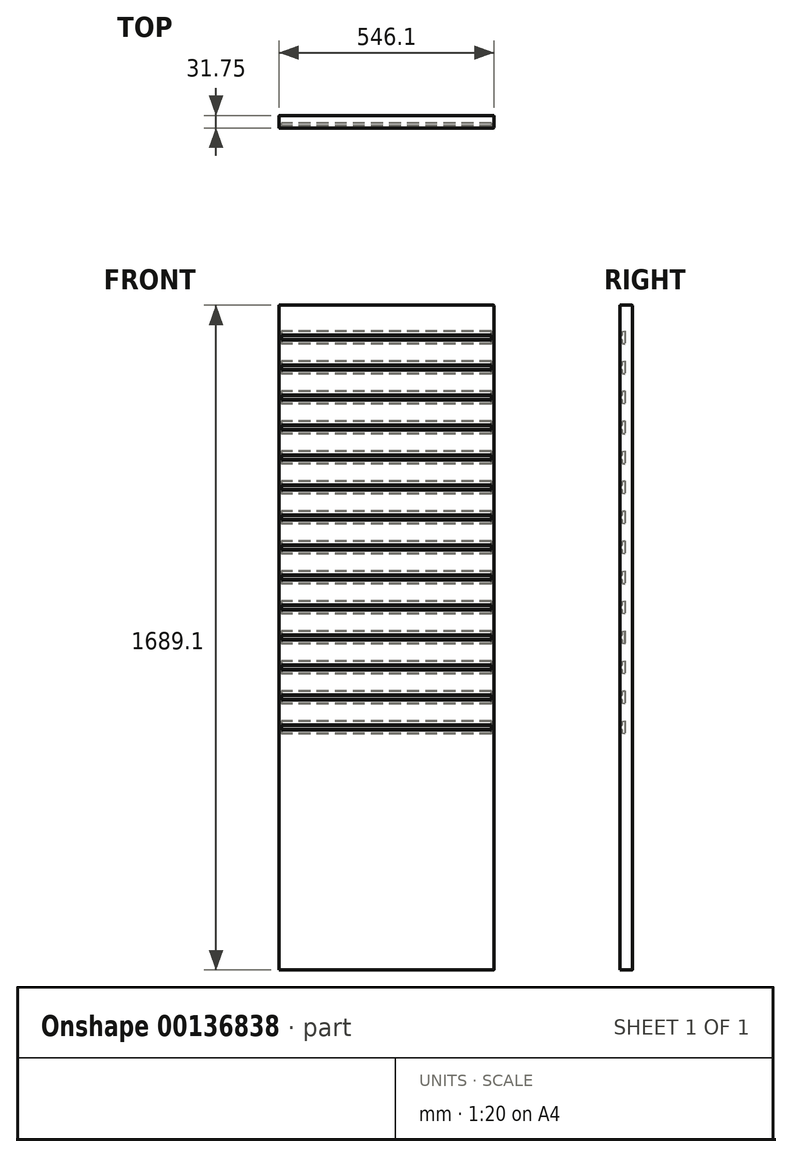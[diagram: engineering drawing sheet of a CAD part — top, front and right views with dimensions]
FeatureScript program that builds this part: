
annotation { "Feature Type Name" : "Feature", "Feature Type Description" : "" }
export const myFeature = defineFeature(function(context is Context, id is Id, definition is map)
    precondition{}
    {
        {
            var Q0;
            Q0=qCreatedBy(makeId("Front.planeOp"),FACE);
            var sketch = newSketch(context, id + "F0", { "sketchPlane" : qUnion([Q0])});
            skLineSegment(sketch, "E0.bottom", {"start": v(266.7, -841.38) * mm, "end": v(-266.7, -841.38) * mm});
            skLineSegment(sketch, "E0.top", {"start": v(266.7, 841.37) * mm, "end": v(-266.7, 841.37) * mm});
            skLineSegment(sketch, "E0.left", {"start": v(266.7, -841.38) * mm, "end": v(266.7, 841.37) * mm});
            skLineSegment(sketch, "E0.right", {"start": v(-266.7, -841.38) * mm, "end": v(-266.7, 841.37) * mm});
            skPoint(sketch, "E0.middle", {"position": v(0, 0) * mm});
            skSolve(sketch);
        }
        {
            var Q0;
            Q0=makeQuery(id+"F0.imprint","IMPRINT",FACE,{"disambiguationData":[TD([[makeQuery(id+"F0.imprint","IMPRINT",EDGE,{"derivedFrom":sQuery(id+"F0.wireOp",EDGE,"E0.bottom")}),-1.0]])]});
            extrude(context, id + "F1", {"entities" : qUnion([Q0]), "oppositeDirection" : true, "depth" : 31.75 * mm});
        }
        {
            var Q0;
            Q0=makeQuery(id+"F1.opExtrude","SWEPT_FACE",FACE,{"disambiguationData":[OSD([sQuery(id+"F0.wireOp",EDGE,"E0.left")])]});
            var sketch = newSketch(context, id + "F2", { "sketchPlane" : qUnion([Q0])});
            skLineSegment(sketch, "E1", {"start": v(-4.76, -4.76) * mm, "end": v(-3.18, -4.76) * mm});
            skLineSegment(sketch, "E2", {"start": v(-6.35, -6.35) * mm, "end": v(-4.76, -4.76) * mm});
            skLineSegment(sketch, "E3", {"start": v(-3.18, -4.76) * mm, "end": v(0, -6.6) * mm});
            skLineSegment(sketch, "E4", {"start": v(-3.18, 4.76) * mm, "end": v(0, 6.6) * mm});
            skLineSegment(sketch, "E5", {"start": v(-4.76, 4.76) * mm, "end": v(-3.18, 4.76) * mm});
            skLineSegment(sketch, "E6", {"start": v(-6.35, 6.35) * mm, "end": v(-4.76, 4.76) * mm});
            skLineSegment(sketch, "E7", {"start": v(0, 14.97) * mm, "end": v(0, 6.6) * mm});
            skLineSegment(sketch, "E8", {"start": v(6.35, 16.67) * mm, "end": v(6.35, -16.67) * mm});
            skLineSegment(sketch, "E9", {"start": v(6.35, -16.67) * mm, "end": v(0, -14.97) * mm});
            skLineSegment(sketch, "E10", {"start": v(0, -6.6) * mm, "end": v(0, -14.97) * mm});
            skLineSegment(sketch, "E11", {"start": v(6.35, 16.67) * mm, "end": v(0, 14.97) * mm});
            skLineSegment(sketch, "E12", {"start": v(-6.35, 6.35) * mm, "end": v(-6.35, -6.35) * mm});
            skSolve(sketch);
        }
        {
            var Q0;
            Q0 = qSketchRegion(id + "F2", true);
            extrude(context, id + "F3", {"entities" : qUnion([Q0]), "depth" : 635 * mm});
        }
        {
            var Q0;
            Q0=makeQuery(id+"F3.opExtrude","CAP_FACE",FACE,{"disambiguationData":[OSD([sQuery(id+"F2.wireOp",EDGE,"E1"),sQuery(id+"F2.wireOp",EDGE,"E2"),sQuery(id+"F2.wireOp",EDGE,"E3"),sQuery(id+"F2.wireOp",EDGE,"E4"),sQuery(id+"F2.wireOp",EDGE,"E5"),sQuery(id+"F2.wireOp",EDGE,"E6"),sQuery(id+"F2.wireOp",EDGE,"E7"),sQuery(id+"F2.wireOp",EDGE,"E9"),sQuery(id+"F2.wireOp",EDGE,"E10"),sQuery(id+"F2.wireOp",EDGE,"E11"),sQuery(id+"F2.wireOp",EDGE,"E8"),sQuery(id+"F2.wireOp",EDGE,"E12")])],"isStart":false});
            var sketch = newSketch(context, id + "F4", { "sketchPlane" : qUnion([Q0])});
            skPoint(sketch, "E13", {"position": v(-6.35, 0) * mm});
            skSolve(sketch);
        }
        {
            var Q0;
            Q0=makeQuery(id+"F1.opExtrude","SWEPT_FACE",FACE,{"disambiguationData":[OSD([sQuery(id+"F0.wireOp",EDGE,"E0.left")])]});
            var sketch = newSketch(context, id + "F5", { "sketchPlane" : qUnion([Q0])});
            skPoint(sketch, "E14", {"position": v(0, 765.17) * mm});
            skPoint(sketch, "E15.0.1.0", {"position": v(0, 688.97) * mm});
            skPoint(sketch, "E15.0.2.0", {"position": v(0, 612.77) * mm});
            skPoint(sketch, "E15.0.3.0", {"position": v(0, 536.57) * mm});
            skPoint(sketch, "E15.0.4.0", {"position": v(0, 460.37) * mm});
            skPoint(sketch, "E15.0.5.0", {"position": v(0, 384.17) * mm});
            skPoint(sketch, "E15.0.6.0", {"position": v(0, 307.97) * mm});
            skPoint(sketch, "E15.0.7.0", {"position": v(0, 231.77) * mm});
            skPoint(sketch, "E15.0.8.0", {"position": v(0, 155.57) * mm});
            skPoint(sketch, "E15.0.9.0", {"position": v(0, 79.37) * mm});
            skLineSegment(sketch, "E15.direction1", {"start": v(0, 765.17) * mm, "end": v(25.4, 765.17) * mm, "construction": true});
            skLineSegment(sketch, "E15.direction2", {"start": v(0, 765.17) * mm, "end": v(0, 688.97) * mm, "construction": true});
            skPoint(sketch, "E16.0.0.10", {"position": v(0, 3.17) * mm});
            skPoint(sketch, "E16.0.0.11", {"position": v(0, -73.03) * mm});
            skPoint(sketch, "E16.0.0.12", {"position": v(0, -149.23) * mm});
            skPoint(sketch, "E16.0.0.13", {"position": v(0, -225.43) * mm});
            skSolve(sketch);
        }
        {
            var Q0;
            Q0=makeQuery(id+"F3.opExtrude","SWEPT_BODY",BODY,{"disambiguationData":[OSD([sQuery(id+"F2.wireOp",EDGE,"E1"),sQuery(id+"F2.wireOp",EDGE,"E2"),sQuery(id+"F2.wireOp",EDGE,"E3"),sQuery(id+"F2.wireOp",EDGE,"E4"),sQuery(id+"F2.wireOp",EDGE,"E5"),sQuery(id+"F2.wireOp",EDGE,"E6"),sQuery(id+"F2.wireOp",EDGE,"E7"),sQuery(id+"F2.wireOp",EDGE,"E9"),sQuery(id+"F2.wireOp",EDGE,"E10"),sQuery(id+"F2.wireOp",EDGE,"E11"),sQuery(id+"F2.wireOp",EDGE,"E8"),sQuery(id+"F2.wireOp",EDGE,"E12")])]});
            var Q1;
            Q1=sQuery(id+"F4.wireOp",VERTEX,"E13");
            var Q2;
            Q2=sQuery(id+"F5.wireOp",VERTEX,"E16.0.0.13");
            transform(context, id + "F6", {"entities" : qUnion([Q0]), "transformType" : TransformType.TRANSLATION_ENTITY, "oppositeDirectionEntity" : false, "transformLine" : qUnion([Q1, Q2]), "makeCopy" : true});
        }
        {
            var Q0;
            Q0=makeQuery(id+"F3.opExtrude","SWEPT_BODY",BODY,{"disambiguationData":[OSD([sQuery(id+"F2.wireOp",EDGE,"E1"),sQuery(id+"F2.wireOp",EDGE,"E2"),sQuery(id+"F2.wireOp",EDGE,"E3"),sQuery(id+"F2.wireOp",EDGE,"E4"),sQuery(id+"F2.wireOp",EDGE,"E5"),sQuery(id+"F2.wireOp",EDGE,"E6"),sQuery(id+"F2.wireOp",EDGE,"E7"),sQuery(id+"F2.wireOp",EDGE,"E9"),sQuery(id+"F2.wireOp",EDGE,"E10"),sQuery(id+"F2.wireOp",EDGE,"E11"),sQuery(id+"F2.wireOp",EDGE,"E8"),sQuery(id+"F2.wireOp",EDGE,"E12")])]});
            var Q1;
            Q1=sQuery(id+"F4.wireOp",VERTEX,"E13");
            var Q2;
            Q2=sQuery(id+"F5.wireOp",VERTEX,"E16.0.0.12");
            transform(context, id + "F7", {"entities" : qUnion([Q0]), "transformType" : TransformType.TRANSLATION_ENTITY, "oppositeDirectionEntity" : false, "transformLine" : qUnion([Q1, Q2]), "makeCopy" : true});
        }
        {
            var Q0;
            Q0=makeQuery(id+"F3.opExtrude","SWEPT_BODY",BODY,{"disambiguationData":[OSD([sQuery(id+"F2.wireOp",EDGE,"E1"),sQuery(id+"F2.wireOp",EDGE,"E2"),sQuery(id+"F2.wireOp",EDGE,"E3"),sQuery(id+"F2.wireOp",EDGE,"E4"),sQuery(id+"F2.wireOp",EDGE,"E5"),sQuery(id+"F2.wireOp",EDGE,"E6"),sQuery(id+"F2.wireOp",EDGE,"E7"),sQuery(id+"F2.wireOp",EDGE,"E9"),sQuery(id+"F2.wireOp",EDGE,"E10"),sQuery(id+"F2.wireOp",EDGE,"E11"),sQuery(id+"F2.wireOp",EDGE,"E8"),sQuery(id+"F2.wireOp",EDGE,"E12")])]});
            var Q1;
            Q1=sQuery(id+"F4.wireOp",VERTEX,"E13");
            var Q2;
            Q2=sQuery(id+"F5.wireOp",VERTEX,"E16.0.0.11");
            transform(context, id + "F8", {"entities" : qUnion([Q0]), "transformType" : TransformType.TRANSLATION_ENTITY, "oppositeDirectionEntity" : false, "transformLine" : qUnion([Q1, Q2]), "makeCopy" : true});
        }
        {
            var Q0;
            Q0=makeQuery(id+"F3.opExtrude","SWEPT_BODY",BODY,{"disambiguationData":[OSD([sQuery(id+"F2.wireOp",EDGE,"E1"),sQuery(id+"F2.wireOp",EDGE,"E2"),sQuery(id+"F2.wireOp",EDGE,"E3"),sQuery(id+"F2.wireOp",EDGE,"E4"),sQuery(id+"F2.wireOp",EDGE,"E5"),sQuery(id+"F2.wireOp",EDGE,"E6"),sQuery(id+"F2.wireOp",EDGE,"E7"),sQuery(id+"F2.wireOp",EDGE,"E9"),sQuery(id+"F2.wireOp",EDGE,"E10"),sQuery(id+"F2.wireOp",EDGE,"E11"),sQuery(id+"F2.wireOp",EDGE,"E8"),sQuery(id+"F2.wireOp",EDGE,"E12")])]});
            var Q1;
            Q1=sQuery(id+"F4.wireOp",VERTEX,"E13");
            var Q2;
            Q2=sQuery(id+"F5.wireOp",VERTEX,"E16.0.0.10");
            transform(context, id + "F9", {"entities" : qUnion([Q0]), "transformType" : TransformType.TRANSLATION_ENTITY, "oppositeDirectionEntity" : false, "transformLine" : qUnion([Q1, Q2]), "makeCopy" : true});
        }
        {
            var Q0;
            Q0=makeQuery(id+"F3.opExtrude","SWEPT_BODY",BODY,{"disambiguationData":[OSD([sQuery(id+"F2.wireOp",EDGE,"E1"),sQuery(id+"F2.wireOp",EDGE,"E2"),sQuery(id+"F2.wireOp",EDGE,"E3"),sQuery(id+"F2.wireOp",EDGE,"E4"),sQuery(id+"F2.wireOp",EDGE,"E5"),sQuery(id+"F2.wireOp",EDGE,"E6"),sQuery(id+"F2.wireOp",EDGE,"E7"),sQuery(id+"F2.wireOp",EDGE,"E9"),sQuery(id+"F2.wireOp",EDGE,"E10"),sQuery(id+"F2.wireOp",EDGE,"E11"),sQuery(id+"F2.wireOp",EDGE,"E8"),sQuery(id+"F2.wireOp",EDGE,"E12")])]});
            var Q1;
            Q1=sQuery(id+"F4.wireOp",VERTEX,"E13");
            var Q2;
            Q2=sQuery(id+"F5.wireOp",VERTEX,"E15.0.9.0");
            transform(context, id + "F10", {"entities" : qUnion([Q0]), "transformType" : TransformType.TRANSLATION_ENTITY, "oppositeDirectionEntity" : false, "transformLine" : qUnion([Q1, Q2]), "makeCopy" : true});
        }
        {
            var Q0;
            Q0=makeQuery(id+"F3.opExtrude","SWEPT_BODY",BODY,{"disambiguationData":[OSD([sQuery(id+"F2.wireOp",EDGE,"E1"),sQuery(id+"F2.wireOp",EDGE,"E2"),sQuery(id+"F2.wireOp",EDGE,"E3"),sQuery(id+"F2.wireOp",EDGE,"E4"),sQuery(id+"F2.wireOp",EDGE,"E5"),sQuery(id+"F2.wireOp",EDGE,"E6"),sQuery(id+"F2.wireOp",EDGE,"E7"),sQuery(id+"F2.wireOp",EDGE,"E9"),sQuery(id+"F2.wireOp",EDGE,"E10"),sQuery(id+"F2.wireOp",EDGE,"E11"),sQuery(id+"F2.wireOp",EDGE,"E8"),sQuery(id+"F2.wireOp",EDGE,"E12")])]});
            var Q1;
            Q1=sQuery(id+"F4.wireOp",VERTEX,"E13");
            var Q2;
            Q2=sQuery(id+"F5.wireOp",VERTEX,"E15.0.8.0");
            transform(context, id + "F11", {"entities" : qUnion([Q0]), "transformType" : TransformType.TRANSLATION_ENTITY, "oppositeDirectionEntity" : false, "transformLine" : qUnion([Q1, Q2]), "makeCopy" : true});
        }
        {
            var Q0;
            Q0=makeQuery(id+"F3.opExtrude","SWEPT_BODY",BODY,{"disambiguationData":[OSD([sQuery(id+"F2.wireOp",EDGE,"E1"),sQuery(id+"F2.wireOp",EDGE,"E2"),sQuery(id+"F2.wireOp",EDGE,"E3"),sQuery(id+"F2.wireOp",EDGE,"E4"),sQuery(id+"F2.wireOp",EDGE,"E5"),sQuery(id+"F2.wireOp",EDGE,"E6"),sQuery(id+"F2.wireOp",EDGE,"E7"),sQuery(id+"F2.wireOp",EDGE,"E9"),sQuery(id+"F2.wireOp",EDGE,"E10"),sQuery(id+"F2.wireOp",EDGE,"E11"),sQuery(id+"F2.wireOp",EDGE,"E8"),sQuery(id+"F2.wireOp",EDGE,"E12")])]});
            var Q1;
            Q1=sQuery(id+"F4.wireOp",VERTEX,"E13");
            var Q2;
            Q2=sQuery(id+"F5.wireOp",VERTEX,"E15.0.7.0");
            transform(context, id + "F12", {"entities" : qUnion([Q0]), "transformType" : TransformType.TRANSLATION_ENTITY, "oppositeDirectionEntity" : false, "transformLine" : qUnion([Q1, Q2]), "makeCopy" : true});
        }
        {
            var Q0;
            Q0=makeQuery(id+"F3.opExtrude","SWEPT_BODY",BODY,{"disambiguationData":[OSD([sQuery(id+"F2.wireOp",EDGE,"E1"),sQuery(id+"F2.wireOp",EDGE,"E2"),sQuery(id+"F2.wireOp",EDGE,"E3"),sQuery(id+"F2.wireOp",EDGE,"E4"),sQuery(id+"F2.wireOp",EDGE,"E5"),sQuery(id+"F2.wireOp",EDGE,"E6"),sQuery(id+"F2.wireOp",EDGE,"E7"),sQuery(id+"F2.wireOp",EDGE,"E9"),sQuery(id+"F2.wireOp",EDGE,"E10"),sQuery(id+"F2.wireOp",EDGE,"E11"),sQuery(id+"F2.wireOp",EDGE,"E8"),sQuery(id+"F2.wireOp",EDGE,"E12")])]});
            var Q1;
            Q1=sQuery(id+"F4.wireOp",VERTEX,"E13");
            var Q2;
            Q2=sQuery(id+"F5.wireOp",VERTEX,"E15.0.6.0");
            transform(context, id + "F13", {"entities" : qUnion([Q0]), "transformType" : TransformType.TRANSLATION_ENTITY, "oppositeDirectionEntity" : false, "transformLine" : qUnion([Q1, Q2]), "makeCopy" : true});
        }
        {
            var Q0;
            Q0=makeQuery(id+"F3.opExtrude","SWEPT_BODY",BODY,{"disambiguationData":[OSD([sQuery(id+"F2.wireOp",EDGE,"E1"),sQuery(id+"F2.wireOp",EDGE,"E2"),sQuery(id+"F2.wireOp",EDGE,"E3"),sQuery(id+"F2.wireOp",EDGE,"E4"),sQuery(id+"F2.wireOp",EDGE,"E5"),sQuery(id+"F2.wireOp",EDGE,"E6"),sQuery(id+"F2.wireOp",EDGE,"E7"),sQuery(id+"F2.wireOp",EDGE,"E9"),sQuery(id+"F2.wireOp",EDGE,"E10"),sQuery(id+"F2.wireOp",EDGE,"E11"),sQuery(id+"F2.wireOp",EDGE,"E8"),sQuery(id+"F2.wireOp",EDGE,"E12")])]});
            var Q1;
            Q1=sQuery(id+"F4.wireOp",VERTEX,"E13");
            var Q2;
            Q2=sQuery(id+"F5.wireOp",VERTEX,"E15.0.5.0");
            transform(context, id + "F14", {"entities" : qUnion([Q0]), "transformType" : TransformType.TRANSLATION_ENTITY, "oppositeDirectionEntity" : false, "transformLine" : qUnion([Q1, Q2]), "makeCopy" : true});
        }
        {
            var Q0;
            Q0=makeQuery(id+"F3.opExtrude","SWEPT_BODY",BODY,{"disambiguationData":[OSD([sQuery(id+"F2.wireOp",EDGE,"E1"),sQuery(id+"F2.wireOp",EDGE,"E2"),sQuery(id+"F2.wireOp",EDGE,"E3"),sQuery(id+"F2.wireOp",EDGE,"E4"),sQuery(id+"F2.wireOp",EDGE,"E5"),sQuery(id+"F2.wireOp",EDGE,"E6"),sQuery(id+"F2.wireOp",EDGE,"E7"),sQuery(id+"F2.wireOp",EDGE,"E9"),sQuery(id+"F2.wireOp",EDGE,"E10"),sQuery(id+"F2.wireOp",EDGE,"E11"),sQuery(id+"F2.wireOp",EDGE,"E8"),sQuery(id+"F2.wireOp",EDGE,"E12")])]});
            var Q1;
            Q1=sQuery(id+"F4.wireOp",VERTEX,"E13");
            var Q2;
            Q2=sQuery(id+"F5.wireOp",VERTEX,"E15.0.4.0");
            transform(context, id + "F15", {"entities" : qUnion([Q0]), "transformType" : TransformType.TRANSLATION_ENTITY, "oppositeDirectionEntity" : false, "transformLine" : qUnion([Q1, Q2]), "makeCopy" : true});
        }
        {
            var Q0;
            Q0=makeQuery(id+"F3.opExtrude","SWEPT_BODY",BODY,{"disambiguationData":[OSD([sQuery(id+"F2.wireOp",EDGE,"E1"),sQuery(id+"F2.wireOp",EDGE,"E2"),sQuery(id+"F2.wireOp",EDGE,"E3"),sQuery(id+"F2.wireOp",EDGE,"E4"),sQuery(id+"F2.wireOp",EDGE,"E5"),sQuery(id+"F2.wireOp",EDGE,"E6"),sQuery(id+"F2.wireOp",EDGE,"E7"),sQuery(id+"F2.wireOp",EDGE,"E9"),sQuery(id+"F2.wireOp",EDGE,"E10"),sQuery(id+"F2.wireOp",EDGE,"E11"),sQuery(id+"F2.wireOp",EDGE,"E8"),sQuery(id+"F2.wireOp",EDGE,"E12")])]});
            var Q1;
            Q1=sQuery(id+"F4.wireOp",VERTEX,"E13");
            var Q2;
            Q2=sQuery(id+"F5.wireOp",VERTEX,"E15.0.3.0");
            transform(context, id + "F16", {"entities" : qUnion([Q0]), "transformType" : TransformType.TRANSLATION_ENTITY, "oppositeDirectionEntity" : false, "transformLine" : qUnion([Q1, Q2]), "makeCopy" : true});
        }
        {
            var Q0;
            Q0=makeQuery(id+"F3.opExtrude","SWEPT_BODY",BODY,{"disambiguationData":[OSD([sQuery(id+"F2.wireOp",EDGE,"E1"),sQuery(id+"F2.wireOp",EDGE,"E2"),sQuery(id+"F2.wireOp",EDGE,"E3"),sQuery(id+"F2.wireOp",EDGE,"E4"),sQuery(id+"F2.wireOp",EDGE,"E5"),sQuery(id+"F2.wireOp",EDGE,"E6"),sQuery(id+"F2.wireOp",EDGE,"E7"),sQuery(id+"F2.wireOp",EDGE,"E9"),sQuery(id+"F2.wireOp",EDGE,"E10"),sQuery(id+"F2.wireOp",EDGE,"E11"),sQuery(id+"F2.wireOp",EDGE,"E8"),sQuery(id+"F2.wireOp",EDGE,"E12")])]});
            var Q1;
            Q1=sQuery(id+"F4.wireOp",VERTEX,"E13");
            var Q2;
            Q2=sQuery(id+"F5.wireOp",VERTEX,"E15.0.2.0");
            transform(context, id + "F17", {"entities" : qUnion([Q0]), "transformType" : TransformType.TRANSLATION_ENTITY, "oppositeDirectionEntity" : false, "transformLine" : qUnion([Q1, Q2]), "makeCopy" : true});
        }
        {
            var Q0;
            Q0=makeQuery(id+"F3.opExtrude","SWEPT_BODY",BODY,{"disambiguationData":[OSD([sQuery(id+"F2.wireOp",EDGE,"E1"),sQuery(id+"F2.wireOp",EDGE,"E2"),sQuery(id+"F2.wireOp",EDGE,"E3"),sQuery(id+"F2.wireOp",EDGE,"E4"),sQuery(id+"F2.wireOp",EDGE,"E5"),sQuery(id+"F2.wireOp",EDGE,"E6"),sQuery(id+"F2.wireOp",EDGE,"E7"),sQuery(id+"F2.wireOp",EDGE,"E9"),sQuery(id+"F2.wireOp",EDGE,"E10"),sQuery(id+"F2.wireOp",EDGE,"E11"),sQuery(id+"F2.wireOp",EDGE,"E8"),sQuery(id+"F2.wireOp",EDGE,"E12")])]});
            var Q1;
            Q1=sQuery(id+"F4.wireOp",VERTEX,"E13");
            var Q2;
            Q2=sQuery(id+"F5.wireOp",VERTEX,"E15.0.1.0");
            transform(context, id + "F18", {"entities" : qUnion([Q0]), "transformType" : TransformType.TRANSLATION_ENTITY, "oppositeDirectionEntity" : false, "transformLine" : qUnion([Q1, Q2]), "makeCopy" : true});
        }
        {
            var Q0;
            Q0=makeQuery(id+"F3.opExtrude","SWEPT_BODY",BODY,{"disambiguationData":[OSD([sQuery(id+"F2.wireOp",EDGE,"E1"),sQuery(id+"F2.wireOp",EDGE,"E2"),sQuery(id+"F2.wireOp",EDGE,"E3"),sQuery(id+"F2.wireOp",EDGE,"E4"),sQuery(id+"F2.wireOp",EDGE,"E5"),sQuery(id+"F2.wireOp",EDGE,"E6"),sQuery(id+"F2.wireOp",EDGE,"E7"),sQuery(id+"F2.wireOp",EDGE,"E9"),sQuery(id+"F2.wireOp",EDGE,"E10"),sQuery(id+"F2.wireOp",EDGE,"E11"),sQuery(id+"F2.wireOp",EDGE,"E8"),sQuery(id+"F2.wireOp",EDGE,"E12")])]});
            var Q1;
            Q1=sQuery(id+"F4.wireOp",VERTEX,"E13");
            var Q2;
            Q2=sQuery(id+"F5.wireOp",VERTEX,"E14");
            transform(context, id + "F19", {"entities" : qUnion([Q0]), "transformType" : TransformType.TRANSLATION_ENTITY, "oppositeDirectionEntity" : false, "transformLine" : qUnion([Q1, Q2]), "makeCopy" : false});
        }
        {
            var Q0;
            Q0=makeQuery(id+"F3.opExtrude","SWEPT_BODY",BODY,{"disambiguationData":[OSD([sQuery(id+"F2.wireOp",EDGE,"E1"),sQuery(id+"F2.wireOp",EDGE,"E2"),sQuery(id+"F2.wireOp",EDGE,"E3"),sQuery(id+"F2.wireOp",EDGE,"E4"),sQuery(id+"F2.wireOp",EDGE,"E5"),sQuery(id+"F2.wireOp",EDGE,"E6"),sQuery(id+"F2.wireOp",EDGE,"E7"),sQuery(id+"F2.wireOp",EDGE,"E9"),sQuery(id+"F2.wireOp",EDGE,"E10"),sQuery(id+"F2.wireOp",EDGE,"E11"),sQuery(id+"F2.wireOp",EDGE,"E8"),sQuery(id+"F2.wireOp",EDGE,"E12")])]});
            var Q1;
            Q1=makeQuery(id+"F18.opPattern","COPY",BODY,{"derivedFrom":makeQuery(id+"F3.opExtrude","SWEPT_BODY",BODY,{"disambiguationData":[OSD([sQuery(id+"F2.wireOp",EDGE,"E1"),sQuery(id+"F2.wireOp",EDGE,"E2"),sQuery(id+"F2.wireOp",EDGE,"E3"),sQuery(id+"F2.wireOp",EDGE,"E4"),sQuery(id+"F2.wireOp",EDGE,"E5"),sQuery(id+"F2.wireOp",EDGE,"E6"),sQuery(id+"F2.wireOp",EDGE,"E7"),sQuery(id+"F2.wireOp",EDGE,"E9"),sQuery(id+"F2.wireOp",EDGE,"E10"),sQuery(id+"F2.wireOp",EDGE,"E11"),sQuery(id+"F2.wireOp",EDGE,"E8"),sQuery(id+"F2.wireOp",EDGE,"E12")])]}),"instanceName":"1"});
            var Q2;
            Q2=makeQuery(id+"F17.opPattern","COPY",BODY,{"derivedFrom":makeQuery(id+"F3.opExtrude","SWEPT_BODY",BODY,{"disambiguationData":[OSD([sQuery(id+"F2.wireOp",EDGE,"E1"),sQuery(id+"F2.wireOp",EDGE,"E2"),sQuery(id+"F2.wireOp",EDGE,"E3"),sQuery(id+"F2.wireOp",EDGE,"E4"),sQuery(id+"F2.wireOp",EDGE,"E5"),sQuery(id+"F2.wireOp",EDGE,"E6"),sQuery(id+"F2.wireOp",EDGE,"E7"),sQuery(id+"F2.wireOp",EDGE,"E9"),sQuery(id+"F2.wireOp",EDGE,"E10"),sQuery(id+"F2.wireOp",EDGE,"E11"),sQuery(id+"F2.wireOp",EDGE,"E8"),sQuery(id+"F2.wireOp",EDGE,"E12")])]}),"instanceName":"1"});
            var Q3;
            Q3=makeQuery(id+"F16.opPattern","COPY",BODY,{"derivedFrom":makeQuery(id+"F3.opExtrude","SWEPT_BODY",BODY,{"disambiguationData":[OSD([sQuery(id+"F2.wireOp",EDGE,"E1"),sQuery(id+"F2.wireOp",EDGE,"E2"),sQuery(id+"F2.wireOp",EDGE,"E3"),sQuery(id+"F2.wireOp",EDGE,"E4"),sQuery(id+"F2.wireOp",EDGE,"E5"),sQuery(id+"F2.wireOp",EDGE,"E6"),sQuery(id+"F2.wireOp",EDGE,"E7"),sQuery(id+"F2.wireOp",EDGE,"E9"),sQuery(id+"F2.wireOp",EDGE,"E10"),sQuery(id+"F2.wireOp",EDGE,"E11"),sQuery(id+"F2.wireOp",EDGE,"E8"),sQuery(id+"F2.wireOp",EDGE,"E12")])]}),"instanceName":"1"});
            var Q4;
            Q4=makeQuery(id+"F15.opPattern","COPY",BODY,{"derivedFrom":makeQuery(id+"F3.opExtrude","SWEPT_BODY",BODY,{"disambiguationData":[OSD([sQuery(id+"F2.wireOp",EDGE,"E1"),sQuery(id+"F2.wireOp",EDGE,"E2"),sQuery(id+"F2.wireOp",EDGE,"E3"),sQuery(id+"F2.wireOp",EDGE,"E4"),sQuery(id+"F2.wireOp",EDGE,"E5"),sQuery(id+"F2.wireOp",EDGE,"E6"),sQuery(id+"F2.wireOp",EDGE,"E7"),sQuery(id+"F2.wireOp",EDGE,"E9"),sQuery(id+"F2.wireOp",EDGE,"E10"),sQuery(id+"F2.wireOp",EDGE,"E11"),sQuery(id+"F2.wireOp",EDGE,"E8"),sQuery(id+"F2.wireOp",EDGE,"E12")])]}),"instanceName":"1"});
            var Q5;
            Q5=makeQuery(id+"F14.opPattern","COPY",BODY,{"derivedFrom":makeQuery(id+"F3.opExtrude","SWEPT_BODY",BODY,{"disambiguationData":[OSD([sQuery(id+"F2.wireOp",EDGE,"E1"),sQuery(id+"F2.wireOp",EDGE,"E2"),sQuery(id+"F2.wireOp",EDGE,"E3"),sQuery(id+"F2.wireOp",EDGE,"E4"),sQuery(id+"F2.wireOp",EDGE,"E5"),sQuery(id+"F2.wireOp",EDGE,"E6"),sQuery(id+"F2.wireOp",EDGE,"E7"),sQuery(id+"F2.wireOp",EDGE,"E9"),sQuery(id+"F2.wireOp",EDGE,"E10"),sQuery(id+"F2.wireOp",EDGE,"E11"),sQuery(id+"F2.wireOp",EDGE,"E8"),sQuery(id+"F2.wireOp",EDGE,"E12")])]}),"instanceName":"1"});
            var Q6;
            Q6=makeQuery(id+"F13.opPattern","COPY",BODY,{"derivedFrom":makeQuery(id+"F3.opExtrude","SWEPT_BODY",BODY,{"disambiguationData":[OSD([sQuery(id+"F2.wireOp",EDGE,"E1"),sQuery(id+"F2.wireOp",EDGE,"E2"),sQuery(id+"F2.wireOp",EDGE,"E3"),sQuery(id+"F2.wireOp",EDGE,"E4"),sQuery(id+"F2.wireOp",EDGE,"E5"),sQuery(id+"F2.wireOp",EDGE,"E6"),sQuery(id+"F2.wireOp",EDGE,"E7"),sQuery(id+"F2.wireOp",EDGE,"E9"),sQuery(id+"F2.wireOp",EDGE,"E10"),sQuery(id+"F2.wireOp",EDGE,"E11"),sQuery(id+"F2.wireOp",EDGE,"E8"),sQuery(id+"F2.wireOp",EDGE,"E12")])]}),"instanceName":"1"});
            var Q7;
            Q7=makeQuery(id+"F12.opPattern","COPY",BODY,{"derivedFrom":makeQuery(id+"F3.opExtrude","SWEPT_BODY",BODY,{"disambiguationData":[OSD([sQuery(id+"F2.wireOp",EDGE,"E1"),sQuery(id+"F2.wireOp",EDGE,"E2"),sQuery(id+"F2.wireOp",EDGE,"E3"),sQuery(id+"F2.wireOp",EDGE,"E4"),sQuery(id+"F2.wireOp",EDGE,"E5"),sQuery(id+"F2.wireOp",EDGE,"E6"),sQuery(id+"F2.wireOp",EDGE,"E7"),sQuery(id+"F2.wireOp",EDGE,"E9"),sQuery(id+"F2.wireOp",EDGE,"E10"),sQuery(id+"F2.wireOp",EDGE,"E11"),sQuery(id+"F2.wireOp",EDGE,"E8"),sQuery(id+"F2.wireOp",EDGE,"E12")])]}),"instanceName":"1"});
            var Q8;
            Q8=makeQuery(id+"F11.opPattern","COPY",BODY,{"derivedFrom":makeQuery(id+"F3.opExtrude","SWEPT_BODY",BODY,{"disambiguationData":[OSD([sQuery(id+"F2.wireOp",EDGE,"E1"),sQuery(id+"F2.wireOp",EDGE,"E2"),sQuery(id+"F2.wireOp",EDGE,"E3"),sQuery(id+"F2.wireOp",EDGE,"E4"),sQuery(id+"F2.wireOp",EDGE,"E5"),sQuery(id+"F2.wireOp",EDGE,"E6"),sQuery(id+"F2.wireOp",EDGE,"E7"),sQuery(id+"F2.wireOp",EDGE,"E9"),sQuery(id+"F2.wireOp",EDGE,"E10"),sQuery(id+"F2.wireOp",EDGE,"E11"),sQuery(id+"F2.wireOp",EDGE,"E8"),sQuery(id+"F2.wireOp",EDGE,"E12")])]}),"instanceName":"1"});
            var Q9;
            Q9=makeQuery(id+"F10.opPattern","COPY",BODY,{"derivedFrom":makeQuery(id+"F3.opExtrude","SWEPT_BODY",BODY,{"disambiguationData":[OSD([sQuery(id+"F2.wireOp",EDGE,"E1"),sQuery(id+"F2.wireOp",EDGE,"E2"),sQuery(id+"F2.wireOp",EDGE,"E3"),sQuery(id+"F2.wireOp",EDGE,"E4"),sQuery(id+"F2.wireOp",EDGE,"E5"),sQuery(id+"F2.wireOp",EDGE,"E6"),sQuery(id+"F2.wireOp",EDGE,"E7"),sQuery(id+"F2.wireOp",EDGE,"E9"),sQuery(id+"F2.wireOp",EDGE,"E10"),sQuery(id+"F2.wireOp",EDGE,"E11"),sQuery(id+"F2.wireOp",EDGE,"E8"),sQuery(id+"F2.wireOp",EDGE,"E12")])]}),"instanceName":"1"});
            var Q10;
            Q10=makeQuery(id+"F9.opPattern","COPY",BODY,{"derivedFrom":makeQuery(id+"F3.opExtrude","SWEPT_BODY",BODY,{"disambiguationData":[OSD([sQuery(id+"F2.wireOp",EDGE,"E1"),sQuery(id+"F2.wireOp",EDGE,"E2"),sQuery(id+"F2.wireOp",EDGE,"E3"),sQuery(id+"F2.wireOp",EDGE,"E4"),sQuery(id+"F2.wireOp",EDGE,"E5"),sQuery(id+"F2.wireOp",EDGE,"E6"),sQuery(id+"F2.wireOp",EDGE,"E7"),sQuery(id+"F2.wireOp",EDGE,"E9"),sQuery(id+"F2.wireOp",EDGE,"E10"),sQuery(id+"F2.wireOp",EDGE,"E11"),sQuery(id+"F2.wireOp",EDGE,"E8"),sQuery(id+"F2.wireOp",EDGE,"E12")])]}),"instanceName":"1"});
            var Q11;
            Q11=makeQuery(id+"F8.opPattern","COPY",BODY,{"derivedFrom":makeQuery(id+"F3.opExtrude","SWEPT_BODY",BODY,{"disambiguationData":[OSD([sQuery(id+"F2.wireOp",EDGE,"E1"),sQuery(id+"F2.wireOp",EDGE,"E2"),sQuery(id+"F2.wireOp",EDGE,"E3"),sQuery(id+"F2.wireOp",EDGE,"E4"),sQuery(id+"F2.wireOp",EDGE,"E5"),sQuery(id+"F2.wireOp",EDGE,"E6"),sQuery(id+"F2.wireOp",EDGE,"E7"),sQuery(id+"F2.wireOp",EDGE,"E9"),sQuery(id+"F2.wireOp",EDGE,"E10"),sQuery(id+"F2.wireOp",EDGE,"E11"),sQuery(id+"F2.wireOp",EDGE,"E8"),sQuery(id+"F2.wireOp",EDGE,"E12")])]}),"instanceName":"1"});
            var Q12;
            Q12=makeQuery(id+"F7.opPattern","COPY",BODY,{"derivedFrom":makeQuery(id+"F3.opExtrude","SWEPT_BODY",BODY,{"disambiguationData":[OSD([sQuery(id+"F2.wireOp",EDGE,"E1"),sQuery(id+"F2.wireOp",EDGE,"E2"),sQuery(id+"F2.wireOp",EDGE,"E3"),sQuery(id+"F2.wireOp",EDGE,"E4"),sQuery(id+"F2.wireOp",EDGE,"E5"),sQuery(id+"F2.wireOp",EDGE,"E6"),sQuery(id+"F2.wireOp",EDGE,"E7"),sQuery(id+"F2.wireOp",EDGE,"E9"),sQuery(id+"F2.wireOp",EDGE,"E10"),sQuery(id+"F2.wireOp",EDGE,"E11"),sQuery(id+"F2.wireOp",EDGE,"E8"),sQuery(id+"F2.wireOp",EDGE,"E12")])]}),"instanceName":"1"});
            var Q13;
            Q13=makeQuery(id+"F6.opPattern","COPY",BODY,{"derivedFrom":makeQuery(id+"F3.opExtrude","SWEPT_BODY",BODY,{"disambiguationData":[OSD([sQuery(id+"F2.wireOp",EDGE,"E1"),sQuery(id+"F2.wireOp",EDGE,"E2"),sQuery(id+"F2.wireOp",EDGE,"E3"),sQuery(id+"F2.wireOp",EDGE,"E4"),sQuery(id+"F2.wireOp",EDGE,"E5"),sQuery(id+"F2.wireOp",EDGE,"E6"),sQuery(id+"F2.wireOp",EDGE,"E7"),sQuery(id+"F2.wireOp",EDGE,"E9"),sQuery(id+"F2.wireOp",EDGE,"E10"),sQuery(id+"F2.wireOp",EDGE,"E11"),sQuery(id+"F2.wireOp",EDGE,"E8"),sQuery(id+"F2.wireOp",EDGE,"E12")])]}),"instanceName":"1"});
            var Q14;
            Q14=makeQuery(id+"F1.opExtrude","SWEPT_BODY",BODY,{"disambiguationData":[OSD([sQuery(id+"F0.wireOp",EDGE,"E0.bottom"),sQuery(id+"F0.wireOp",EDGE,"E0.top"),sQuery(id+"F0.wireOp",EDGE,"E0.left"),sQuery(id+"F0.wireOp",EDGE,"E0.right")])]});
            booleanBodies(context, id + "F20", {"operationType" : BooleanOperationType.SUBTRACTION, "tools" : qUnion([Q0, Q1, Q2, Q3, Q4, Q5, Q6, Q7, Q8, Q9, Q10, Q11, Q12, Q13]), "targets" : qUnion([Q14])});
        }
        {
            var Q0;
            Q0=makeQuery(id+"F1.opExtrude","SWEPT_FACE",FACE,{"disambiguationData":[OSD([sQuery(id+"F0.wireOp",EDGE,"E0.left")])]});
            var sketch = newSketch(context, id + "F21", { "sketchPlane" : qUnion([Q0])});
            skLineSegment(sketch, "E17.bottom", {"start": v(31.75, -841.38) * mm, "end": v(0, -841.38) * mm});
            skLineSegment(sketch, "E17.top", {"start": v(31.75, 841.37) * mm, "end": v(0, 841.37) * mm});
            skLineSegment(sketch, "E17.left", {"start": v(31.75, -841.38) * mm, "end": v(31.75, 841.37) * mm});
            skLineSegment(sketch, "E17.right", {"start": v(0, -841.38) * mm, "end": v(0, 841.37) * mm});
            skSolve(sketch);
        }
        {
            var Q0;
            Q0 = qSketchRegion(id + "F21", true);
            extrude(context, id + "F22", {"entities" : qUnion([Q0]), "operationType" : NewBodyOperationType.ADD, "depth" : 6.35 * mm});
        }
        {
            var Q0;
            Q0=makeQuery(id+"F1.opExtrude","SWEPT_FACE",FACE,{"disambiguationData":[OSD([sQuery(id+"F0.wireOp",EDGE,"E0.right")])]});
            var sketch = newSketch(context, id + "F23", { "sketchPlane" : qUnion([Q0])});
            skLineSegment(sketch, "E18.bottom", {"start": v(-31.75, 841.37) * mm, "end": v(0, 841.37) * mm});
            skLineSegment(sketch, "E18.top", {"start": v(-31.75, -841.38) * mm, "end": v(0, -841.38) * mm});
            skLineSegment(sketch, "E18.left", {"start": v(-31.75, 841.37) * mm, "end": v(-31.75, -841.38) * mm});
            skLineSegment(sketch, "E18.right", {"start": v(0, 841.37) * mm, "end": v(0, -841.38) * mm});
            skSolve(sketch);
        }
        {
            var Q0;
            Q0 = qSketchRegion(id + "F23", true);
            extrude(context, id + "F24", {"entities" : qUnion([Q0]), "operationType" : NewBodyOperationType.ADD, "depth" : 6.35 * mm});
        }
        {
            var Q0;
            Q0=makeQuery(id+"F24.boolean.opBoolean","MERGE",FACE,{"derivedFrom":[makeQuery(id+"F22.boolean.opBoolean","MERGE",FACE,{"derivedFrom":[makeQuery(id+"F1.opExtrude","SWEPT_FACE",FACE,{"disambiguationData":[OSD([sQuery(id+"F0.wireOp",EDGE,"E0.top")])]}),makeQuery(id+"F22.opExtrude","SWEPT_FACE",FACE,{"disambiguationData":[OSD([sQuery(id+"F21.wireOp",EDGE,"E17.top")])]})]}),makeQuery(id+"F24.opExtrude","SWEPT_FACE",FACE,{"disambiguationData":[OSD([sQuery(id+"F23.wireOp",EDGE,"E18.bottom")])]})]});
            var sketch = newSketch(context, id + "F25", { "sketchPlane" : qUnion([Q0])});
            skLineSegment(sketch, "E19.0", {"start": v(273.05, 31.75) * mm, "end": v(-273.05, 31.75) * mm});
            skLineSegment(sketch, "E20.0", {"start": v(-273.05, 31.75) * mm, "end": v(-273.05, 0) * mm});
            skLineSegment(sketch, "E21.0", {"start": v(273.05, 0) * mm, "end": v(-273.05, 0) * mm});
            skLineSegment(sketch, "E22.0", {"start": v(273.05, 31.75) * mm, "end": v(273.05, 0) * mm});
            skSolve(sketch);
        }
        {
            var Q0;
            Q0=makeQuery(id+"F25.imprint","IMPRINT",FACE,{"disambiguationData":[TD([[makeQuery(id+"F25.imprint","IMPRINT",EDGE,{"derivedFrom":sQuery(id+"F25.wireOp",EDGE,"E19.0")}),1.0]])]});
            extrude(context, id + "F26", {"entities" : qUnion([Q0]), "operationType" : NewBodyOperationType.ADD, "depth" : 6.35 * mm});
        }
        {
            var Q0;
            Q0=makeQuery(id+"F26.opExtrude","CAP_EDGE",EDGE,{"disambiguationData":[OSD([sQuery(id+"F25.wireOp",EDGE,"E19.0")])],"isStart":false});
            var Q1;
            Q1=makeQuery(id+"F26.opExtrude","CAP_EDGE",EDGE,{"disambiguationData":[OSD([sQuery(id+"F25.wireOp",EDGE,"E21.0")])],"isStart":false});
            var Q2;
            Q2=makeQuery(id+"F26.boolean.opBoolean","MERGE",EDGE,{"derivedFrom":[makeQuery(id+"F24.opExtrude","CAP_EDGE",EDGE,{"disambiguationData":[OSD([sQuery(id+"F23.wireOp",EDGE,"E18.left")])],"isStart":false}),makeQuery(id+"F26.opExtrude","SWEPT_EDGE",EDGE,{"disambiguationData":[OSD([sQuery(id+"F25.wireOp",EDGE,"E19.0"),sQuery(id+"F25.wireOp",EDGE,"E20.0")])]})]});
            var Q3;
            Q3=makeQuery(id+"F26.boolean.opBoolean","MERGE",EDGE,{"derivedFrom":[makeQuery(id+"F24.opExtrude","CAP_EDGE",EDGE,{"disambiguationData":[OSD([sQuery(id+"F23.wireOp",EDGE,"E18.right")])],"isStart":false}),makeQuery(id+"F26.opExtrude","SWEPT_EDGE",EDGE,{"disambiguationData":[OSD([sQuery(id+"F25.wireOp",EDGE,"E20.0"),sQuery(id+"F25.wireOp",EDGE,"E21.0")])]})]});
            var Q4;
            Q4=makeQuery(id+"F26.boolean.opBoolean","MERGE",EDGE,{"derivedFrom":[makeQuery(id+"F22.opExtrude","CAP_EDGE",EDGE,{"disambiguationData":[OSD([sQuery(id+"F21.wireOp",EDGE,"E17.right")])],"isStart":false}),makeQuery(id+"F26.opExtrude","SWEPT_EDGE",EDGE,{"disambiguationData":[OSD([sQuery(id+"F25.wireOp",EDGE,"E21.0"),sQuery(id+"F25.wireOp",EDGE,"E22.0")])]})]});
            var Q5;
            Q5=makeQuery(id+"F26.boolean.opBoolean","MERGE",EDGE,{"derivedFrom":[makeQuery(id+"F22.opExtrude","CAP_EDGE",EDGE,{"disambiguationData":[OSD([sQuery(id+"F21.wireOp",EDGE,"E17.left")])],"isStart":false}),makeQuery(id+"F26.opExtrude","SWEPT_EDGE",EDGE,{"disambiguationData":[OSD([sQuery(id+"F25.wireOp",EDGE,"E19.0"),sQuery(id+"F25.wireOp",EDGE,"E22.0")])]})]});
            var Q6;
            Q6=makeQuery(id+"F26.opExtrude","CAP_EDGE",EDGE,{"disambiguationData":[OSD([sQuery(id+"F25.wireOp",EDGE,"E22.0")])],"isStart":false});
            var Q7;
            Q7=makeQuery(id+"F26.opExtrude","CAP_EDGE",EDGE,{"disambiguationData":[OSD([sQuery(id+"F25.wireOp",EDGE,"E20.0")])],"isStart":false});
            fillet(context, id + "F27", {"entities" : qUnion([Q0, Q1, Q2, Q3, Q4, Q5, Q6, Q7]), "radius" : 1.59 * mm, "tangentPropagation" : true, "allowEdgeOverflow" : false});
        }
    });
